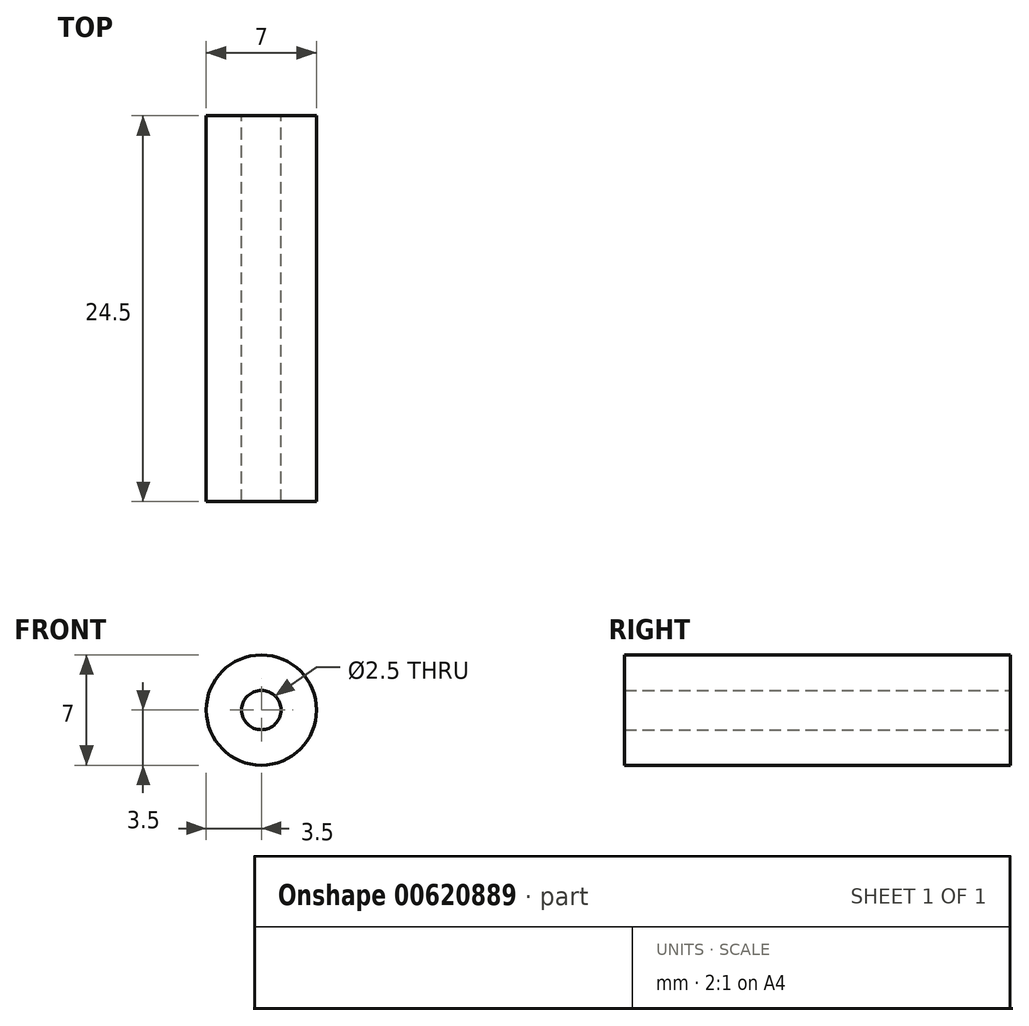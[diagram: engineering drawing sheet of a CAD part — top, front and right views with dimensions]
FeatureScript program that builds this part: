
annotation { "Feature Type Name" : "Feature", "Feature Type Description" : "" }
export const myFeature = defineFeature(function(context is Context, id is Id, definition is map)
    precondition{}
    {
        {
            var Q0;
            Q0=qCreatedBy(makeId("Front.planeOp"),FACE);
            var sketch = newSketch(context, id + "F0", { "sketchPlane" : qUnion([Q0])});
            skCircle(sketch, "E0", {"center": v(0, 0) * mm, "radius": 1.25 * mm});
            skCircle(sketch, "E1", {"center": v(0, 0) * mm, "radius": 3.5 * mm});
            skSolve(sketch);
        }
        {
            var Q0;
            Q0=makeQuery(id+"F0.imprint","IMPRINT",FACE,{"disambiguationData":[TD([[makeQuery(id+"F0.imprint","IMPRINT",EDGE,{"derivedFrom":sQuery(id+"F0.wireOp",EDGE,"E0")}),-1.0]])]});
            extrude(context, id + "F1", {"entities" : qUnion([Q0]), "depth" : 24.5 * mm, "offsetDistance" : 25 * mm});
        }
    });
